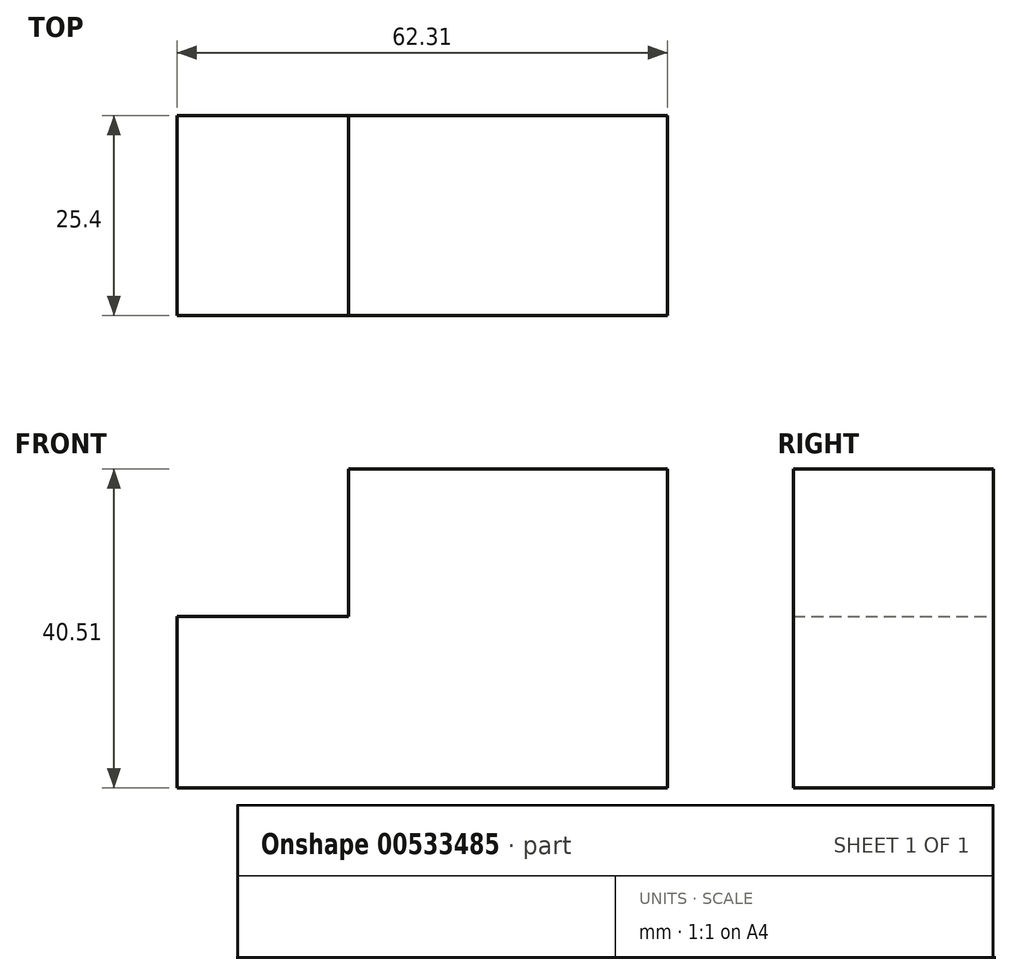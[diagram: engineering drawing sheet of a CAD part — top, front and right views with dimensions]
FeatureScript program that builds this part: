
annotation { "Feature Type Name" : "Feature", "Feature Type Description" : "" }
export const myFeature = defineFeature(function(context is Context, id is Id, definition is map)
    precondition{}
    {
        {
            var Q0;
            Q0=qCreatedBy(makeId("Front.planeOp"),FACE);
            var sketch = newSketch(context, id + "F0", { "sketchPlane" : qUnion([Q0])});
            skLineSegment(sketch, "E0", {"start": v(0, 0) * mm, "end": v(-41.4, 0) * mm});
            skLineSegment(sketch, "E1", {"start": v(-41.4, 0) * mm, "end": v(-41.4, 21.8) * mm});
            skLineSegment(sketch, "E2", {"start": v(-41.4, 21.8) * mm, "end": v(-40.51, 21.8) * mm});
            skLineSegment(sketch, "E3", {"start": v(-40.51, 21.8) * mm, "end": v(-40.51, 40.51) * mm});
            skLineSegment(sketch, "E4", {"start": v(-40.51, 40.51) * mm, "end": v(0, 40.51) * mm});
            skLineSegment(sketch, "E5", {"start": v(0, 40.51) * mm, "end": v(0, 0) * mm});
            skLineSegment(sketch, "E6", {"start": v(-41.4, 0) * mm, "end": v(-62.3, 0) * mm});
            skLineSegment(sketch, "E7", {"start": v(-62.3, 0) * mm, "end": v(-62.3, 21.8) * mm});
            skLineSegment(sketch, "E8", {"start": v(-62.3, 21.8) * mm, "end": v(-40.51, 21.8) * mm});
            skSolve(sketch);
        }
        {
            var Q0;
            Q0 = qSketchRegion(id + "F0", true);
            extrude(context, id + "F1", {"entities" : qUnion([Q0]), "depth" : 25.4 * mm, "offsetDistance" : 25.4 * mm});
        }
    });
